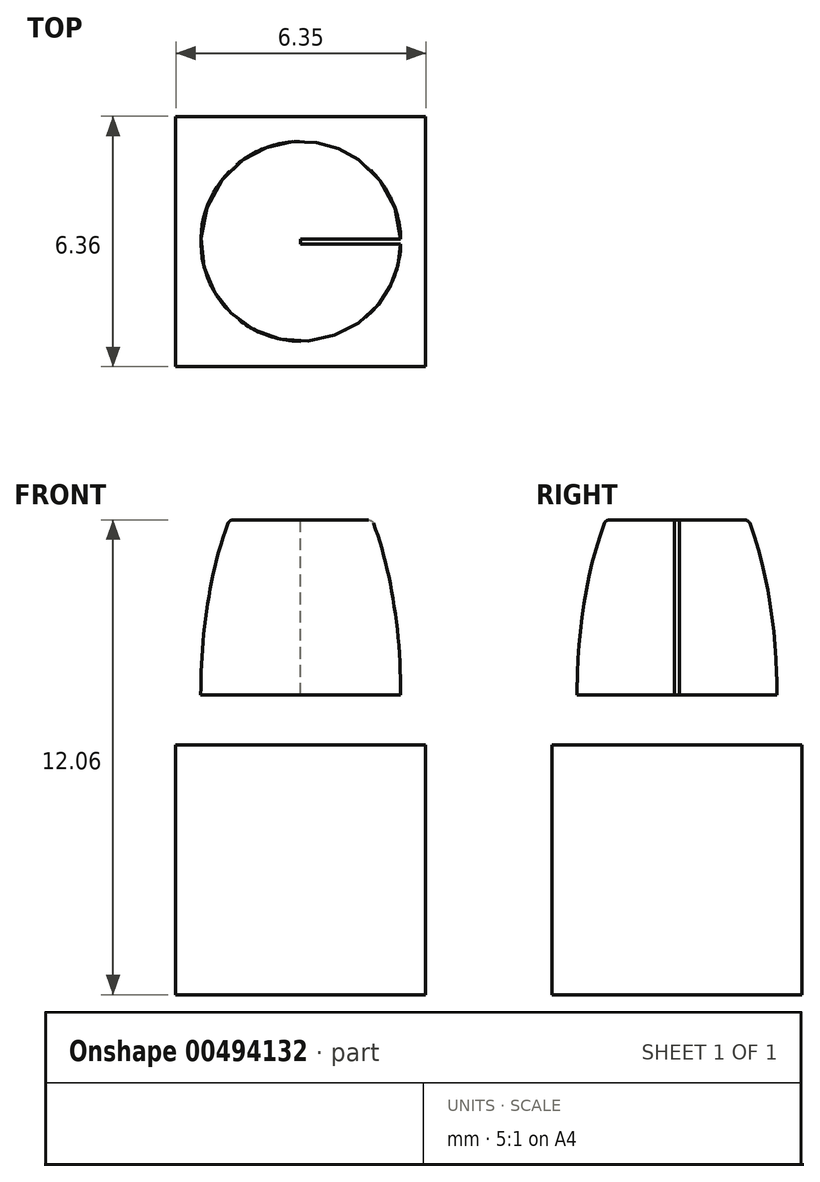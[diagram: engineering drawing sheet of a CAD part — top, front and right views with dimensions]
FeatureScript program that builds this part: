
annotation { "Feature Type Name" : "Feature", "Feature Type Description" : "" }
export const myFeature = defineFeature(function(context is Context, id is Id, definition is map)
    precondition{}
    {
        {
            var Q0;
            Q0=qCreatedBy(makeId("Top.planeOp"),FACE);
            var sketch = newSketch(context, id + "F0", { "sketchPlane" : qUnion([Q0])});
            skLineSegment(sketch, "E0.bottom", {"start": v(-2.86, 3.17) * mm, "end": v(2.86, 3.17) * mm});
            skLineSegment(sketch, "E0.top", {"start": v(-2.86, -3.18) * mm, "end": v(2.86, -3.18) * mm});
            skLineSegment(sketch, "E0.left", {"start": v(-3.17, 2.86) * mm, "end": v(-3.18, -2.86) * mm});
            skLineSegment(sketch, "E0.right", {"start": v(3.18, 2.86) * mm, "end": v(3.17, -2.86) * mm});
            skPoint(sketch, "E0.middle", {"position": v(0, 0) * mm});
            skPoint(sketch, "E1.visualSharp", {"position": v(-3.17, 3.17) * mm});
            skArc(sketch, "E1.filletArc", {"start": v(-2.86, 3.17) * mm, "mid": v(-3.08, 3.08) * mm, "end": v(-3.17, 2.86) * mm});
            skPoint(sketch, "E2.visualSharp", {"position": v(-3.18, -3.18) * mm});
            skArc(sketch, "E2.filletArc", {"start": v(-3.18, -2.86) * mm, "mid": v(-3.08, -3.08) * mm, "end": v(-2.86, -3.18) * mm});
            skPoint(sketch, "E3.visualSharp", {"position": v(3.17, -3.18) * mm});
            skArc(sketch, "E3.filletArc", {"start": v(2.86, -3.18) * mm, "mid": v(3.08, -3.08) * mm, "end": v(3.17, -2.86) * mm});
            skPoint(sketch, "E4.visualSharp", {"position": v(3.18, 3.17) * mm});
            skArc(sketch, "E4.filletArc", {"start": v(3.18, 2.86) * mm, "mid": v(3.08, 3.08) * mm, "end": v(2.86, 3.17) * mm});
            skLineSegment(sketch, "E5", {"start": v(-3.17, 2.86) * mm, "end": v(-3.17, 3.17) * mm});
            skLineSegment(sketch, "E6", {"start": v(-3.17, 3.17) * mm, "end": v(-2.86, 3.17) * mm});
            skLineSegment(sketch, "E7", {"start": v(2.86, 3.17) * mm, "end": v(3.18, 3.17) * mm});
            skLineSegment(sketch, "E8", {"start": v(3.18, 3.17) * mm, "end": v(3.18, 2.86) * mm});
            skLineSegment(sketch, "E9", {"start": v(2.86, -3.18) * mm, "end": v(3.17, -3.18) * mm});
            skLineSegment(sketch, "E10", {"start": v(3.17, -2.86) * mm, "end": v(3.17, -3.18) * mm});
            skLineSegment(sketch, "E11", {"start": v(-3.18, -2.86) * mm, "end": v(-3.18, -3.18) * mm});
            skLineSegment(sketch, "E12", {"start": v(-3.18, -3.18) * mm, "end": v(-2.86, -3.18) * mm});
            skSolve(sketch);
        }
        {
            var Q0;
            Q0 = qSketchRegion(id + "F0", true);
            extrude(context, id + "F1", {"entities" : qUnion([Q0]), "endBound" : BoundingType.SYMMETRIC, "depth" : 6.35 * mm});
        }
        {
            var Q0;
            Q0=qCreatedBy(makeId("Front.planeOp"),FACE);
            var sketch = newSketch(context, id + "F2", { "sketchPlane" : qUnion([Q0])});
            skArc(sketch, "E13.0.0", {"start": v(-2.86, 3.18) * mm, "mid": v(-3.08, 3.08) * mm, "end": v(-3.18, 2.86) * mm});
            skArc(sketch, "E13.0.2", {"start": v(-3.18, 2.86) * mm, "mid": v(-3.08, 3.08) * mm, "end": v(-2.86, 3.18) * mm});
            skLineSegment(sketch, "E14.0.1", {"start": v(-2.86, 3.18) * mm, "end": v(2.86, 3.18) * mm});
            skLineSegment(sketch, "E14.0.3", {"start": v(2.86, 3.18) * mm, "end": v(-2.86, 3.18) * mm});
            skArc(sketch, "E15.0.0", {"start": v(3.17, 2.86) * mm, "mid": v(3.08, 3.08) * mm, "end": v(2.86, 3.18) * mm});
            skArc(sketch, "E15.0.2", {"start": v(2.86, 3.18) * mm, "mid": v(3.08, 3.08) * mm, "end": v(3.17, 2.86) * mm});
            skLineSegment(sketch, "E16", {"start": v(0, 3.18) * mm, "end": v(0, 8.9) * mm});
            skPoint(sketch, "E16.endSnap0", {"position": v(0, 3.18) * mm});
            skLineSegment(sketch, "E17", {"start": v(0, 8.9) * mm, "end": v(1.81, 8.9) * mm});
            skLineSegment(sketch, "E18.bottom", {"start": v(0, 3.18) * mm, "end": v(2.54, 3.18) * mm});
            skLineSegment(sketch, "E18.top", {"start": v(0, 4.45) * mm, "end": v(2.54, 4.45) * mm});
            skLineSegment(sketch, "E18.left", {"start": v(0, 3.18) * mm, "end": v(0, 4.45) * mm});
            skLineSegment(sketch, "E18.right", {"start": v(2.54, 3.18) * mm, "end": v(2.54, 4.45) * mm});
            skLineSegment(sketch, "E19.0.0", {"start": v(-3.18, -3.17) * mm, "end": v(-3.18, 2.86) * mm});
            skLineSegment(sketch, "E19.0.2", {"start": v(-3.17, 2.86) * mm, "end": v(-3.17, -3.17) * mm});
            skLineSegment(sketch, "E20.0.0", {"start": v(3.18, -3.17) * mm, "end": v(3.18, 2.86) * mm});
            skLineSegment(sketch, "E20.0.2", {"start": v(3.17, 2.86) * mm, "end": v(3.17, -3.17) * mm});
            skLineSegment(sketch, "E21.0.0", {"start": v(-2.86, -3.18) * mm, "end": v(-3.18, -3.18) * mm});
            skLineSegment(sketch, "E21.0.2", {"start": v(-3.17, -3.18) * mm, "end": v(-2.86, -3.18) * mm});
            skLineSegment(sketch, "E21.0.3", {"start": v(-2.86, -3.18) * mm, "end": v(2.86, -3.18) * mm});
            skLineSegment(sketch, "E21.0.4", {"start": v(2.86, -3.18) * mm, "end": v(3.18, -3.18) * mm});
            skLineSegment(sketch, "E21.0.6", {"start": v(3.17, -3.18) * mm, "end": v(2.86, -3.18) * mm});
            skLineSegment(sketch, "E21.0.7", {"start": v(2.86, -3.18) * mm, "end": v(-2.86, -3.18) * mm});
            skEllipticalArc(sketch, "E22", {});
            skFitSpline(sketch, "E23.0", {"points": [v(0.32, 10.37) * mm, v(0, 10.44) * mm, v(-0.32, 10.37) * mm, v(-0.7, 10.09) * mm, v(-1.1, 9.56) * mm, v(-1.45, 8.82) * mm, v(-1.76, 7.9) * mm, v(-1.99, 6.83) * mm, v(-2.13, 5.66) * mm, v(-2.18, 4.45) * mm, v(-2.13, 3.23) * mm, v(-1.99, 2.06) * mm, v(-1.76, 0.99) * mm, v(-1.45, 0.07) * mm, v(-1.1, -0.67) * mm, v(-0.7, -1.2) * mm, v(-0.32, -1.48) * mm, v(0, -1.55) * mm, v(0.32, -1.48) * mm, v(0.7, -1.2) * mm, v(1.1, -0.67) * mm, v(1.45, 0.07) * mm, v(1.76, 0.99) * mm, v(1.99, 2.06) * mm, v(2.13, 3.23) * mm, v(2.18, 4.45) * mm, v(2.13, 5.66) * mm, v(1.99, 6.83) * mm, v(1.76, 7.9) * mm, v(1.45, 8.82) * mm, v(1.1, 9.56) * mm, v(0.7, 10.09) * mm, v(0.32, 10.37) * mm, v(0, 10.44) * mm, v(-0.32, 10.37) * mm]});
            skFitSpline(sketch, "E24.0", {"points": [v(0.44, 10.6) * mm, v(0, 10.7) * mm, v(-0.44, 10.6) * mm, v(-0.88, 10.26) * mm, v(-1.31, 9.7) * mm, v(-1.69, 8.92) * mm, v(-2, 7.97) * mm, v(-2.24, 6.87) * mm, v(-2.38, 5.68) * mm, v(-2.43, 4.45) * mm, v(-2.38, 3.2) * mm, v(-2.24, 2.02) * mm, v(-2, 0.92) * mm, v(-1.69, -0.03) * mm, v(-1.31, -0.8) * mm, v(-0.88, -1.37) * mm, v(-0.44, -1.7) * mm, v(0, -1.81) * mm, v(0.44, -1.7) * mm, v(0.88, -1.37) * mm, v(1.31, -0.8) * mm, v(1.69, -0.03) * mm, v(2, 0.92) * mm, v(2.24, 2.02) * mm, v(2.38, 3.2) * mm, v(2.43, 4.45) * mm, v(2.38, 5.68) * mm, v(2.24, 6.87) * mm, v(2, 7.97) * mm, v(1.69, 8.92) * mm, v(1.31, 9.7) * mm, v(0.88, 10.26) * mm, v(0.44, 10.6) * mm, v(0, 10.7) * mm, v(-0.44, 10.6) * mm]});
            skLineSegment(sketch, "E25", {"start": v(1.7, 8.84) * mm, "end": v(1.68, 8.9) * mm});
            skLineSegment(sketch, "E26", {"start": v(1.46, 8.75) * mm, "end": v(1.46, 8.9) * mm});
            const initialGuessF2  = {"E22": [0, 0.004445, 0, 1, 0.00635, 0.00254, 4.71238898038469, 5.487786476995442]};
            skSetInitialGuess(sketch, initialGuessF2);
            skSolve(sketch);
        }
        {
            var Q0;
            Q0=makeQuery(id+"F2.imprint","IMPRINT",FACE,{"disambiguationData":[TD([[makeQuery(id+"F2.imprint","IMPRINT",EDGE,{"derivedFrom":sQuery(id+"F2.wireOp",EDGE,"E18.bottom")}),1.0]])]});
            var Q1;
            {var subQ0=sQuery(id+"F2.wireOp",EDGE,"45745adf-f94e-404d-bc12-fde483d5a78a.0");Q1=makeQuery(id+"F2.imprint","IMPRINT",FACE,{"disambiguationData":[TD([[makeQuery(id+"F2.imprint","IMPRINT",EDGE,{"derivedFrom":subQ0}),-1.0]])]});}
            var Q2;
            {var subQ0=sQuery(id+"F2.wireOp",EDGE,"AdALbvXk-3wPX-6Fpe-rOfn-Via4XpPnjhGq");Q2=makeQuery(id+"F2.imprint","IMPRINT",FACE,{"disambiguationData":[TD([[makeQuery(id+"F2.imprint","IMPRINT",EDGE,{"derivedFrom":subQ0}),1.0]])]});}
            var Q3;
            {var subQ0=sQuery(id+"F2.wireOp",EDGE,"E23.0");Q3=makeQuery(id+"F2.imprint","IMPRINT",FACE,{"disambiguationData":[TD([[makeQuery(id+"F2.imprint","IMPRINT",EDGE,{"derivedFrom":subQ0}),-1.0]])]});}
            var Q4;
            {var subQ0=sQuery(id+"F2.wireOp",EDGE,"E22");Q4=makeQuery(id+"F2.imprint","IMPRINT",FACE,{"disambiguationData":[TD([[makeQuery(id+"F2.imprint","IMPRINT",EDGE,{"derivedFrom":subQ0}),1.0]])]});}
            var Q5;
            Q5=sQuery(id+"F2.wireOp",EDGE,"E16");
            revolve(context, id + "F3", {"operationType" : NewBodyOperationType.ADD, "entities" : qUnion([Q0, Q1, Q2, Q3, Q4]), "axis" : qUnion([Q5]), "revolveType" : RevolveType.FULL});
        }
        {
            var Q0;
            Q0=makeQuery(id+"F3.opRevolve","SWEPT_EDGE",EDGE,{"disambiguationData":[OSD([sQuery(id+"F2.wireOp",EDGE,"E17"),sQuery(id+"F2.wireOp",EDGE,"E22")])]});
            fillet(context, id + "F4", {"entities" : qUnion([Q0]), "radius" : 0.13 * mm, "tangentPropagation" : true, "allowEdgeOverflow" : false});
        }
        {
            var Q0;
            {var subQ0=sQuery(id+"F2.wireOp",EDGE,"E22");Q0=makeQuery(id+"F2.imprint","IMPRINT",FACE,{"disambiguationData":[TD([[makeQuery(id+"F2.imprint","IMPRINT",EDGE,{"derivedFrom":subQ0}),1.0]])]});}
            extrude(context, id + "F5", {"entities" : qUnion([Q0]), "operationType" : NewBodyOperationType.REMOVE, "endBound" : BoundingType.SYMMETRIC, "depth" : 0.13 * mm});
        }
    });
